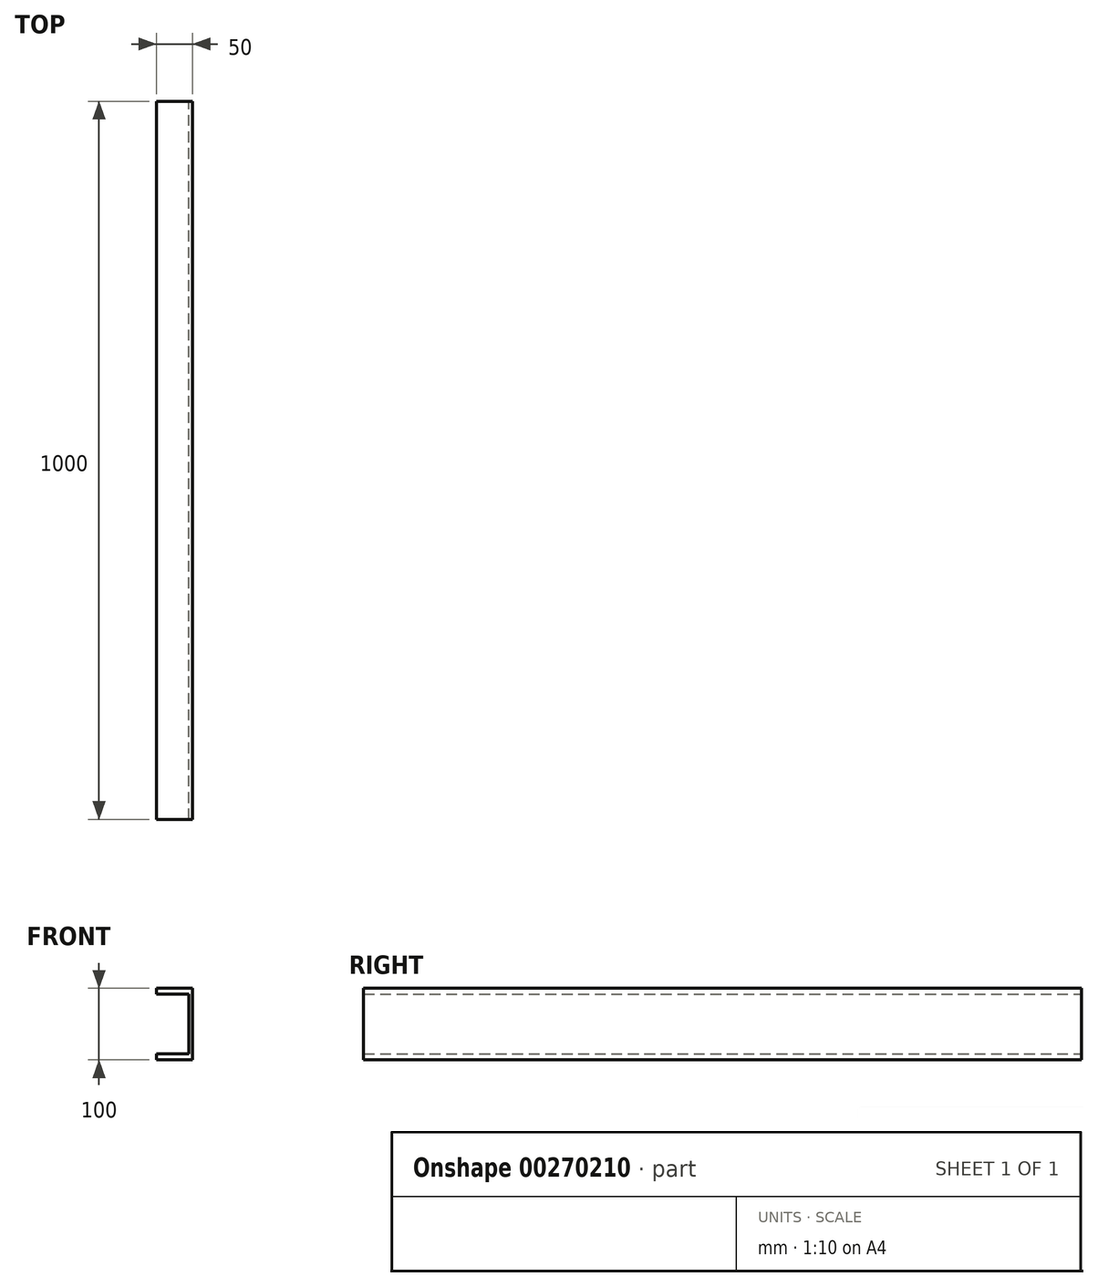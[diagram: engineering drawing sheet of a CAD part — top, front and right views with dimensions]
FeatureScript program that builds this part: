
annotation { "Feature Type Name" : "Feature", "Feature Type Description" : "" }
export const myFeature = defineFeature(function(context is Context, id is Id, definition is map)
    precondition{}
    {
        {
            var Q0;
            Q0=qCreatedBy(makeId("Front.planeOp"),FACE);
            var sketch = newSketch(context, id + "F0", { "sketchPlane" : qUnion([Q0])});
            skLineSegment(sketch, "E0", {"start": v(-44.05, 47.5) * mm, "end": v(5.95, 47.5) * mm});
            skLineSegment(sketch, "E1", {"start": v(5.95, 47.5) * mm, "end": v(5.95, -52.5) * mm});
            skLineSegment(sketch, "E2", {"start": v(5.95, -52.5) * mm, "end": v(-44.05, -52.5) * mm});
            skLineSegment(sketch, "E3", {"start": v(-44.05, 47.5) * mm, "end": v(-44.05, 39) * mm});
            skLineSegment(sketch, "E4", {"start": v(-44.05, 39) * mm, "end": v(0.95, 39) * mm});
            skLineSegment(sketch, "E5", {"start": v(0.95, 39) * mm, "end": v(0.95, -44) * mm});
            skLineSegment(sketch, "E6", {"start": v(0.95, -44) * mm, "end": v(-44.05, -44) * mm});
            skLineSegment(sketch, "E7", {"start": v(-44.05, -44) * mm, "end": v(-44.05, -52.5) * mm});
            skSolve(sketch);
        }
        {
            var Q0;
            Q0=makeQuery(id+"F0.imprint","IMPRINT",FACE,{"disambiguationData":[TD([[makeQuery(id+"F0.imprint","IMPRINT",EDGE,{"derivedFrom":sQuery(id+"F0.wireOp",EDGE,"E0")}),-1.0]])]});
            extrude(context, id + "F1", {"entities" : qUnion([Q0]), "depth" : 1000 * mm});
        }
    });
